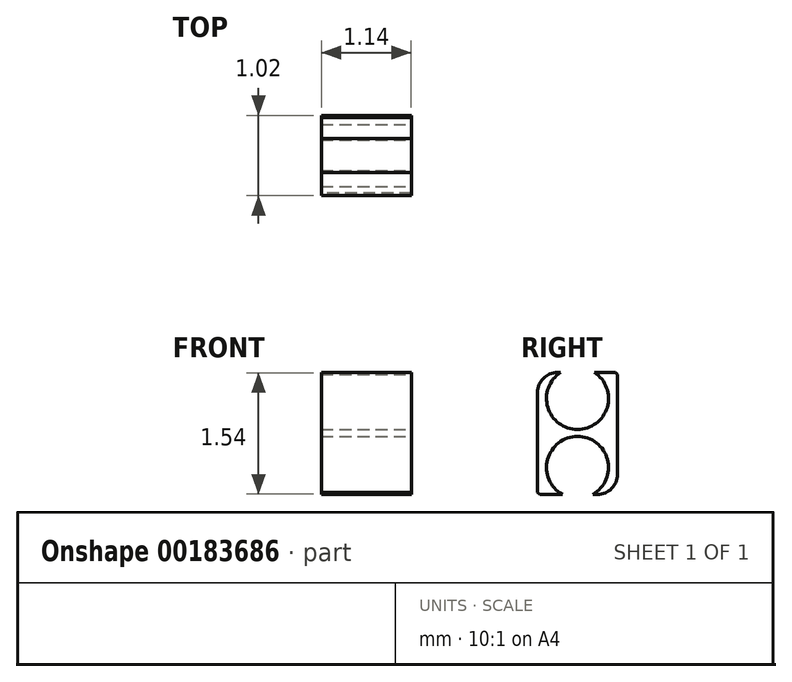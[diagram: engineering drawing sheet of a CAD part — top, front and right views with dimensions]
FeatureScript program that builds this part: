
annotation { "Feature Type Name" : "Feature", "Feature Type Description" : "" }
export const myFeature = defineFeature(function(context is Context, id is Id, definition is map)
    precondition{}
    {
        {
            var Q0;
            Q0=qCreatedBy(makeId("Front.planeOp"),FACE);
            var sketch = newSketch(context, id + "F0", { "sketchPlane" : qUnion([Q0])});
            skLineSegment(sketch, "E0.bottom", {"start": v(-0.57, 0.77) * mm, "end": v(0.57, 0.77) * mm});
            skLineSegment(sketch, "E0.top", {"start": v(-0.57, -0.77) * mm, "end": v(0.57, -0.77) * mm});
            skLineSegment(sketch, "E0.left", {"start": v(-0.57, 0.77) * mm, "end": v(-0.57, -0.77) * mm});
            skLineSegment(sketch, "E0.right", {"start": v(0.57, 0.77) * mm, "end": v(0.57, -0.77) * mm});
            skPoint(sketch, "E0.middle", {"position": v(0, 0) * mm});
            skSolve(sketch);
        }
        {
            var Q0;
            Q0 = qSketchRegion(id + "F0", true);
            extrude(context, id + "F1", {"entities" : qUnion([Q0]), "depth" : 1.02 * mm});
        }
        {
            var Q0;
            Q0=makeQuery(id+"F1.opExtrude","SWEPT_FACE",FACE,{"disambiguationData":[OSD([sQuery(id+"F0.wireOp",EDGE,"E0.right")])]});
            var sketch = newSketch(context, id + "F2", { "sketchPlane" : qUnion([Q0])});
            skLineSegment(sketch, "E1", {"start": v(-0.5, 0.77) * mm, "end": v(-0.5, -0.77) * mm});
            skLineSegment(sketch, "E2", {"start": v(-1.02, 0) * mm, "end": v(0, 0) * mm});
            skCircle(sketch, "E3", {"center": v(-0.5, -0.43) * mm, "radius": 0.4 * mm});
            skCircle(sketch, "E4", {"center": v(-0.5, 0.44) * mm, "radius": 0.4 * mm});
            skSolve(sketch);
        }
        {
            var Q0;
            {var subQ0=sQuery(id+"F2.wireOp",EDGE,"E1");var subQ3=sQuery(id+"F2.wireOp",EDGE,"E4");var subQ4=makeQuery(id+"F2.imprint","INTERSECT",VERTEX,{"derivedFrom":[subQ0,subQ3]});Q0=makeQuery(id+"F2.imprint","IMPRINT",FACE,{"disambiguationData":[TD([[makeQuery(id+"F2.imprint","IMPRINT",EDGE,{"disambiguationData":[TD([[subQ4,1.0]])],"derivedFrom":subQ0}),-1.0]])]});}
            var Q1;
            {var subQ0=sQuery(id+"F2.wireOp",EDGE,"E1");var subQ3=sQuery(id+"F2.wireOp",EDGE,"E3");var subQ4=makeQuery(id+"F2.imprint","INTERSECT",VERTEX,{"derivedFrom":[subQ0,subQ3]});Q1=makeQuery(id+"F2.imprint","IMPRINT",FACE,{"disambiguationData":[TD([[makeQuery(id+"F2.imprint","IMPRINT",EDGE,{"disambiguationData":[TD([[subQ4,-1.0]])],"derivedFrom":subQ0}),-1.0]])]});}
            var Q2;
            {var subQ0=sQuery(id+"F2.wireOp",EDGE,"E1");var subQ3=sQuery(id+"F2.wireOp",EDGE,"E3");var subQ4=makeQuery(id+"F2.imprint","INTERSECT",VERTEX,{"derivedFrom":[subQ0,subQ3]});Q2=makeQuery(id+"F2.imprint","IMPRINT",FACE,{"disambiguationData":[TD([[makeQuery(id+"F2.imprint","IMPRINT",EDGE,{"disambiguationData":[TD([[subQ4,-1.0]])],"derivedFrom":subQ0}),1.0]])]});}
            var Q3;
            {var subQ0=sQuery(id+"F2.wireOp",EDGE,"E1");var subQ3=sQuery(id+"F2.wireOp",EDGE,"E4");var subQ4=makeQuery(id+"F2.imprint","INTERSECT",VERTEX,{"derivedFrom":[subQ0,subQ3]});Q3=makeQuery(id+"F2.imprint","IMPRINT",FACE,{"disambiguationData":[TD([[makeQuery(id+"F2.imprint","IMPRINT",EDGE,{"disambiguationData":[TD([[subQ4,1.0]])],"derivedFrom":subQ0}),1.0]])]});}
            extrude(context, id + "F3", {"entities" : qUnion([Q0, Q1, Q2, Q3]), "operationType" : NewBodyOperationType.REMOVE, "oppositeDirection" : true, "depth" : 25.4 * mm});
        }
        {
            var Q0;
            Q0=makeQuery(id+"F1.opExtrude","CAP_EDGE",EDGE,{"disambiguationData":[OSD([sQuery(id+"F0.wireOp",EDGE,"E0.bottom")])],"isStart":false});
            fillet(context, id + "F4", {"entities" : qUnion([Q0]), "radius" : 0.25 * mm, "tangentPropagation" : true, "allowEdgeOverflow" : false});
        }
        {
            var Q0;
            Q0=makeQuery(id+"F1.opExtrude","CAP_EDGE",EDGE,{"disambiguationData":[OSD([sQuery(id+"F0.wireOp",EDGE,"E0.top")])],"isStart":true});
            fillet(context, id + "F5", {"entities" : qUnion([Q0]), "radius" : 0.25 * mm, "tangentPropagation" : true, "allowEdgeOverflow" : false});
        }
        {
            var Q0;
            Q0=makeQuery(id+"F1.opExtrude","CAP_EDGE",EDGE,{"disambiguationData":[OSD([sQuery(id+"F0.wireOp",EDGE,"E0.bottom")])],"isStart":true});
            var Q1;
            Q1=makeQuery(id+"F1.opExtrude","CAP_EDGE",EDGE,{"disambiguationData":[OSD([sQuery(id+"F0.wireOp",EDGE,"E0.top")])],"isStart":false});
            chamfer(context, id + "F6", {"entities" : qUnion([Q0, Q1]), "width" : 0.03 * mm, "tangentPropagation" : true});
        }
    });
